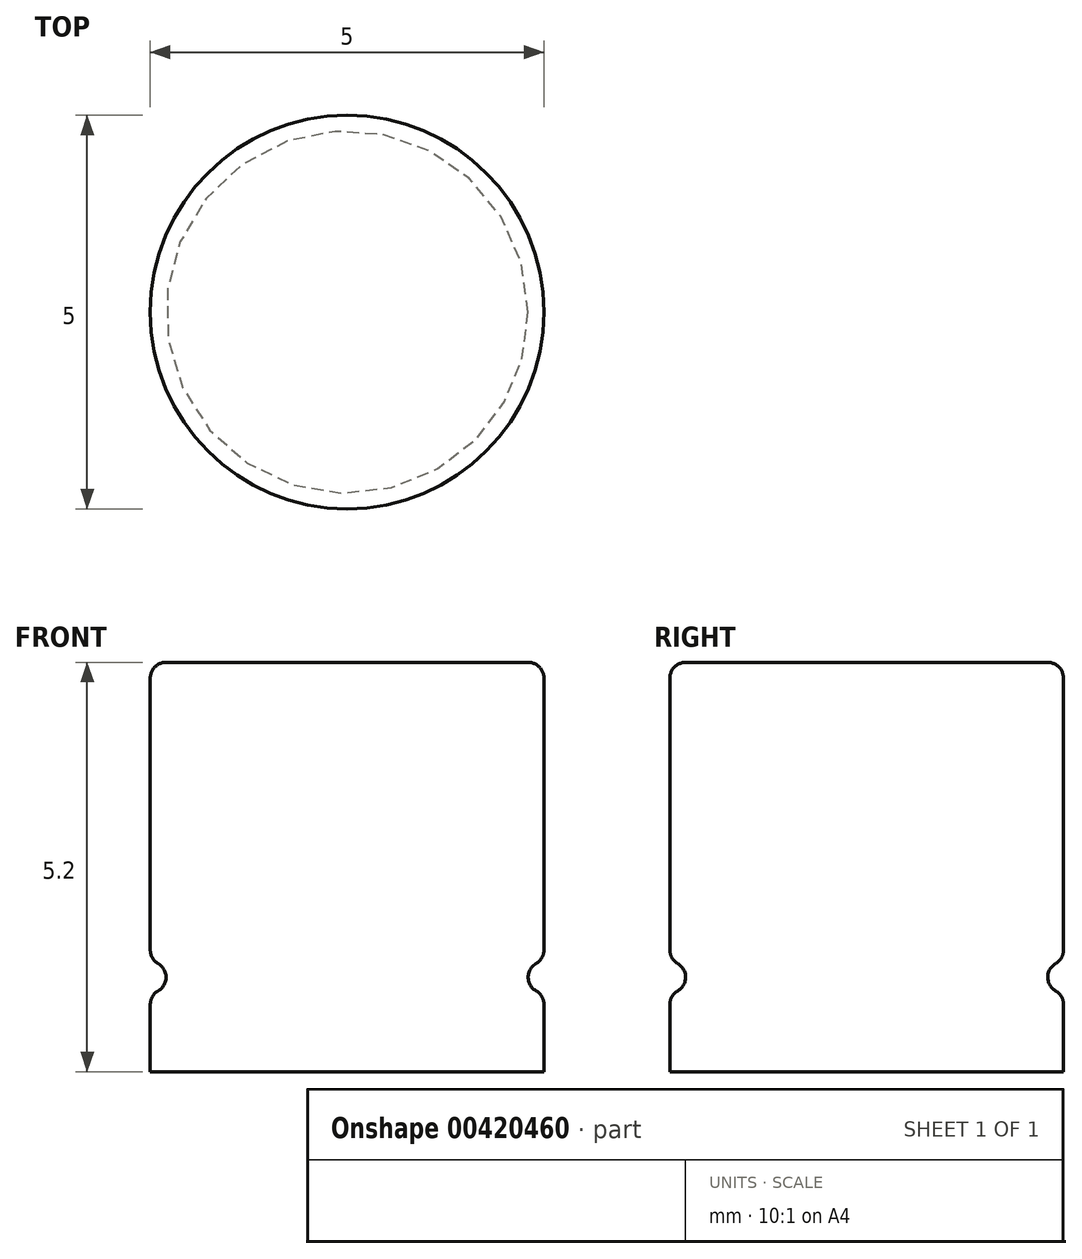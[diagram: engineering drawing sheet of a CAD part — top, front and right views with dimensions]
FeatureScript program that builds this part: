
annotation { "Feature Type Name" : "Feature", "Feature Type Description" : "" }
export const myFeature = defineFeature(function(context is Context, id is Id, definition is map)
    precondition{}
    {
        {
            var Q0;
            Q0=qCreatedBy(makeId("Front.planeOp"),FACE);
            var sketch = newSketch(context, id + "F0", { "sketchPlane" : qUnion([Q0]), "disableImprinting" : false});
            skLineSegment(sketch, "E0.bottom", {"start": v(0, 5.2) * mm, "end": v(2.5, 5.2) * mm});
            skLineSegment(sketch, "E0.top", {"start": v(0, 0) * mm, "end": v(2.5, 0) * mm});
            skLineSegment(sketch, "E0.left", {"start": v(0, 5.2) * mm, "end": v(0, 0) * mm});
            skLineSegment(sketch, "E0.right", {"start": v(2.5, 5.2) * mm, "end": v(2.5, 1.4) * mm});
            skArc(sketch, "E1", {"start": v(2.5, 1.4) * mm, "mid": v(2.3, 1.2) * mm, "end": v(2.5, 1) * mm});
            skLineSegment(sketch, "E2.trimOffspring", {"start": v(2.5, 1) * mm, "end": v(2.5, 0) * mm});
            skLineSegment(sketch, "E3", {"start": v(0, 13.41) * mm, "end": v(0, 0) * mm, "construction": true});
            skSolve(sketch);
        }
        {
            var Q0;
            Q0=makeQuery(id+"F0.imprint","IMPRINT",FACE,{"disambiguationData":[TD([[makeQuery(id+"F0.imprint","IMPRINT",EDGE,{"derivedFrom":sQuery(id+"F0.wireOp",EDGE,"E0.bottom")}),-1.0]])]});
            var Q1;
            Q1=sQuery(id+"F0.wireOp",EDGE,"E3");
            revolve(context, id + "F1", {"entities" : qUnion([Q0]), "axis" : qUnion([Q1]), "revolveType" : RevolveType.FULL});
        }
        {
            var Q0;
            Q0=makeQuery(id+"F1.opRevolve","SWEPT_EDGE",EDGE,{"disambiguationData":[OSD([sQuery(id+"F0.wireOp",EDGE,"E0.right"),sQuery(id+"F0.wireOp",EDGE,"E1")])]});
            var Q1;
            Q1=makeQuery(id+"F1.opRevolve","SWEPT_EDGE",EDGE,{"disambiguationData":[OSD([sQuery(id+"F0.wireOp",EDGE,"E1"),sQuery(id+"F0.wireOp",EDGE,"E2.trimOffspring")])]});
            var Q2;
            Q2=makeQuery(id+"F1.opRevolve","SWEPT_EDGE",EDGE,{"disambiguationData":[OSD([sQuery(id+"F0.wireOp",EDGE,"E0.bottom"),sQuery(id+"F0.wireOp",EDGE,"E0.right")])]});
            fillet(context, id + "F2", {"entities" : qUnion([Q0, Q1, Q2]), "radius" : 0.2 * mm, "tangentPropagation" : true, "allowEdgeOverflow" : false});
        }
    });
